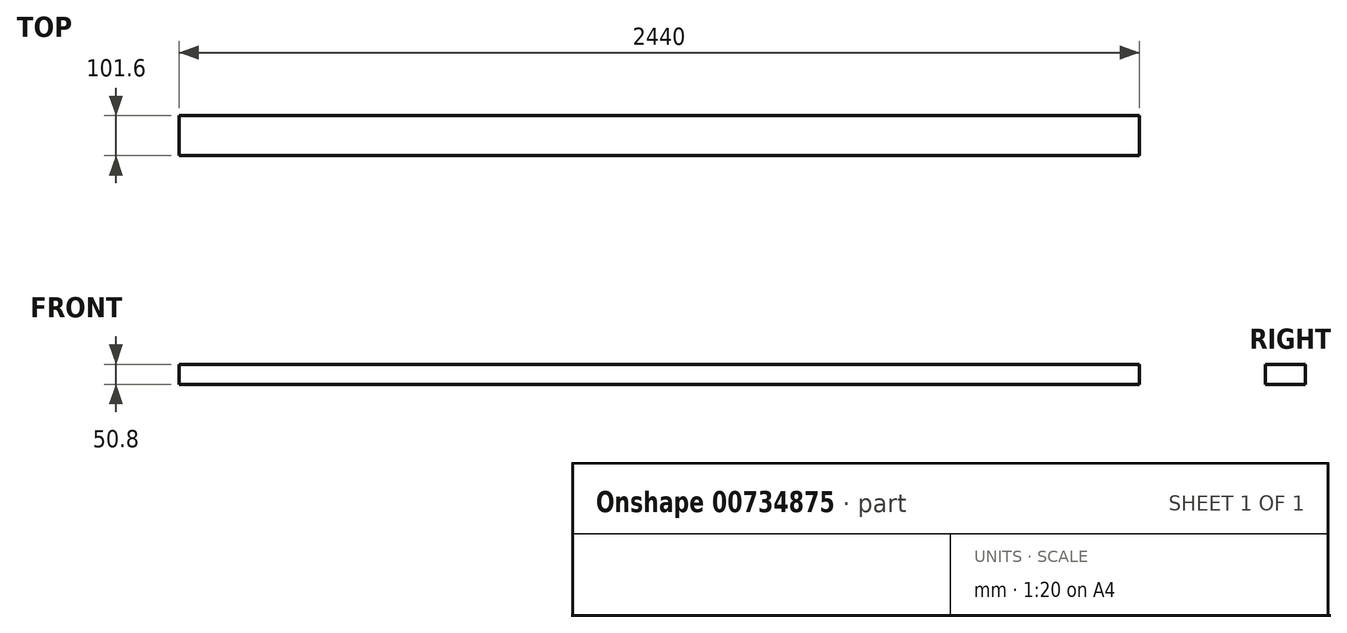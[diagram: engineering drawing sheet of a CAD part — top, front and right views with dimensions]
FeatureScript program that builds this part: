
annotation { "Feature Type Name" : "Feature", "Feature Type Description" : "" }
export const myFeature = defineFeature(function(context is Context, id is Id, definition is map)
    precondition{}
    {
        {
            var Q0;
            Q0=qCreatedBy(makeId("Right.planeOp"),FACE);
            var sketch = newSketch(context, id + "F0", { "sketchPlane" : qUnion([Q0])});
            skLineSegment(sketch, "E0.bottom", {"start": v(-50.8, 25.4) * mm, "end": v(50.8, 25.4) * mm});
            skLineSegment(sketch, "E0.top", {"start": v(-50.8, -25.4) * mm, "end": v(50.8, -25.4) * mm});
            skLineSegment(sketch, "E0.left", {"start": v(-50.8, 25.4) * mm, "end": v(-50.8, -25.4) * mm});
            skLineSegment(sketch, "E0.right", {"start": v(50.8, 25.4) * mm, "end": v(50.8, -25.4) * mm});
            skPoint(sketch, "E0.middle", {"position": v(0, 0) * mm});
            skSolve(sketch);
        }
        {
            var Q0;
            Q0=makeQuery(id+"F0.imprint","IMPRINT",FACE,{"disambiguationData":[TD([[makeQuery(id+"F0.imprint","IMPRINT",EDGE,{"derivedFrom":sQuery(id+"F0.wireOp",EDGE,"E0.bottom")}),-1.0]])]});
            extrude(context, id + "F1", {"entities" : qUnion([Q0]), "endBound" : BoundingType.SYMMETRIC, "depth" : 2440 * mm, "offsetDistance" : 25.4 * mm});
        }
    });
